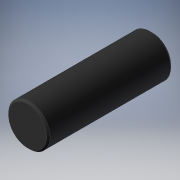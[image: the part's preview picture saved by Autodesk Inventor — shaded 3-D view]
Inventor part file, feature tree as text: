
AUTODESK INVENTOR PART (.ipt)
format: ipt  version: 2019 (Build 230136000, 136)  size: 121,856 bytes
history: native  units: in
note: dims shown in document units (in); Inventor stores cm internally (conversion verified against a paired STEP export)
features: other x35, revolve x1, sketch x1
ambient origin geometry x8: Origin, YZ Plane, XZ Plane, XY Plane, X Axis, Y Axis, Z Axis, Center Point
bodies: Solid1 (feature_tree)
feature tree (37):
  revolve  "Revolution1"  [1 undecoded]
  other  "dia1_XY"
  other  "dia1_YZ"
  other  "dia1_ZX"
  other  "dia1_X"
  other  "dia1_Y"
  other  "dia1_Z"
  other  "dia1_Center"
  other  "dia2_XY"
  other  "dia2_YZ"
  other  "dia2_ZX"
  other  "dia2_X"
  other  "dia2_Y"
  other  "dia2_Z"
  other  "dia2_Center"
  other  "pin_XY"
  other  "pin_YZ"
  other  "pin_ZX"
  other  "pin_X"
  other  "pin_Y"
  other  "pin_Z"
  other  "pin_Center"
  other  "pin1_XY"
  other  "pin1_YZ"
  other  "pin1_ZX"
  other  "pin1_X"
  other  "pin1_Y"
  other  "pin1_Z"
  other  "pin1_Center"
  other  "pin2_XY"
  other  "pin2_YZ"
  other  "pin2_ZX"
  other  "pin2_X"
  other  "pin2_Y"
  other  "pin2_Z"
  other  "pin2_Center"
  sketch  "Sketch_1"  dims[d0=360.0deg]
note: 1 required parameter value undecoded (feature->parameter linkage not recoverable at this tier; creation-order binding heuristic only, values carry confidence <= 0.55)
